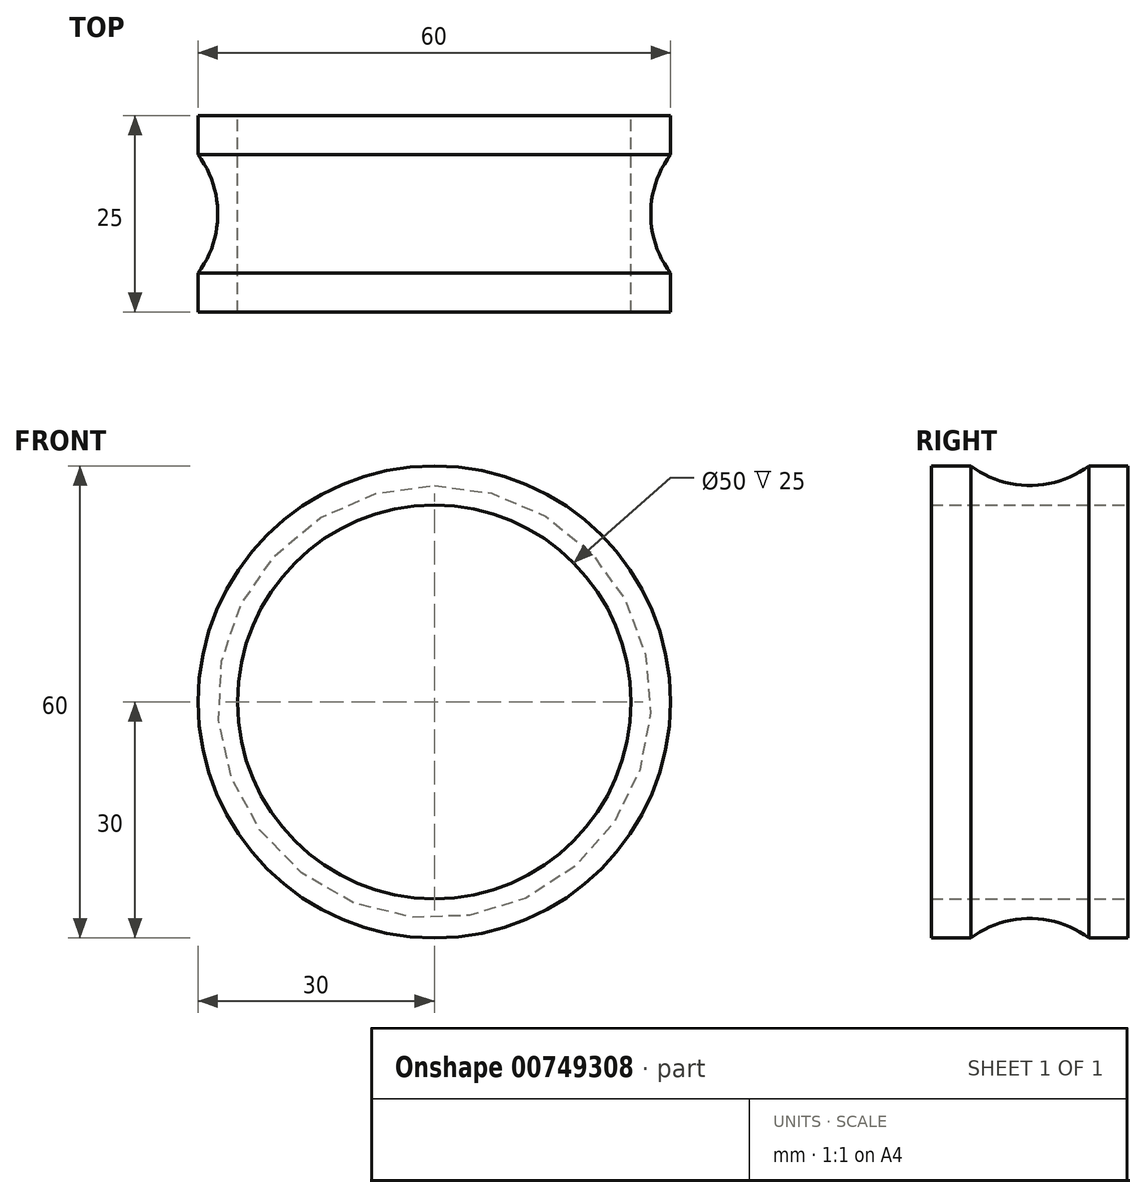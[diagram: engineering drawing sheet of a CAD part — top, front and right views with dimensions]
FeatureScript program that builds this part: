
annotation { "Feature Type Name" : "Feature", "Feature Type Description" : "" }
export const myFeature = defineFeature(function(context is Context, id is Id, definition is map)
    precondition{}
    {
        {
            var Q0;
            Q0=qCreatedBy(makeId("Front.planeOp"),FACE);
            var sketch = newSketch(context, id + "F0", { "sketchPlane" : qUnion([Q0])});
            skCircle(sketch, "E0", {"center": v(0, 0) * mm, "radius": 30 * mm});
            skCircle(sketch, "E1", {"center": v(0, 0) * mm, "radius": 25 * mm});
            skSolve(sketch);
        }
        {
            var Q0;
            Q0=makeQuery(id+"F0.imprint","IMPRINT",FACE,{"disambiguationData":[TD([[makeQuery(id+"F0.imprint","IMPRINT",EDGE,{"derivedFrom":sQuery(id+"F0.wireOp",EDGE,"E0")}),1.0]])]});
            extrude(context, id + "F1", {"entities" : qUnion([Q0]), "depth" : 25 * mm, "offsetDistance" : 25 * mm, "symmetric" : true});
        }
        {
            var Q0;
            Q0=qCreatedBy(makeId("Right.planeOp"),FACE);
            var sketch = newSketch(context, id + "F2", { "sketchPlane" : qUnion([Q0])});
            skCircle(sketch, "E2", {"center": v(0, 40) * mm, "radius": 12.5 * mm});
            skSolve(sketch);
        }
        {
            var Q0;
            Q0=makeQuery(id+"F2.imprint","IMPRINT",FACE,{"disambiguationData":[TD([[makeQuery(id+"F2.imprint","IMPRINT",EDGE,{"derivedFrom":sQuery(id+"F2.wireOp",EDGE,"E2")}),1.0]])]});
            var Q1;
            Q1=sQuery(id+"F0.wireOp",EDGE,"E1");
            revolve(context, id + "F3", {"operationType" : NewBodyOperationType.REMOVE, "surfaceOperationType" : NewSurfaceOperationType.NEW, "entities" : qUnion([Q0]), "axis" : qUnion([Q1]), "revolveType" : RevolveType.FULL});
        }
    });
